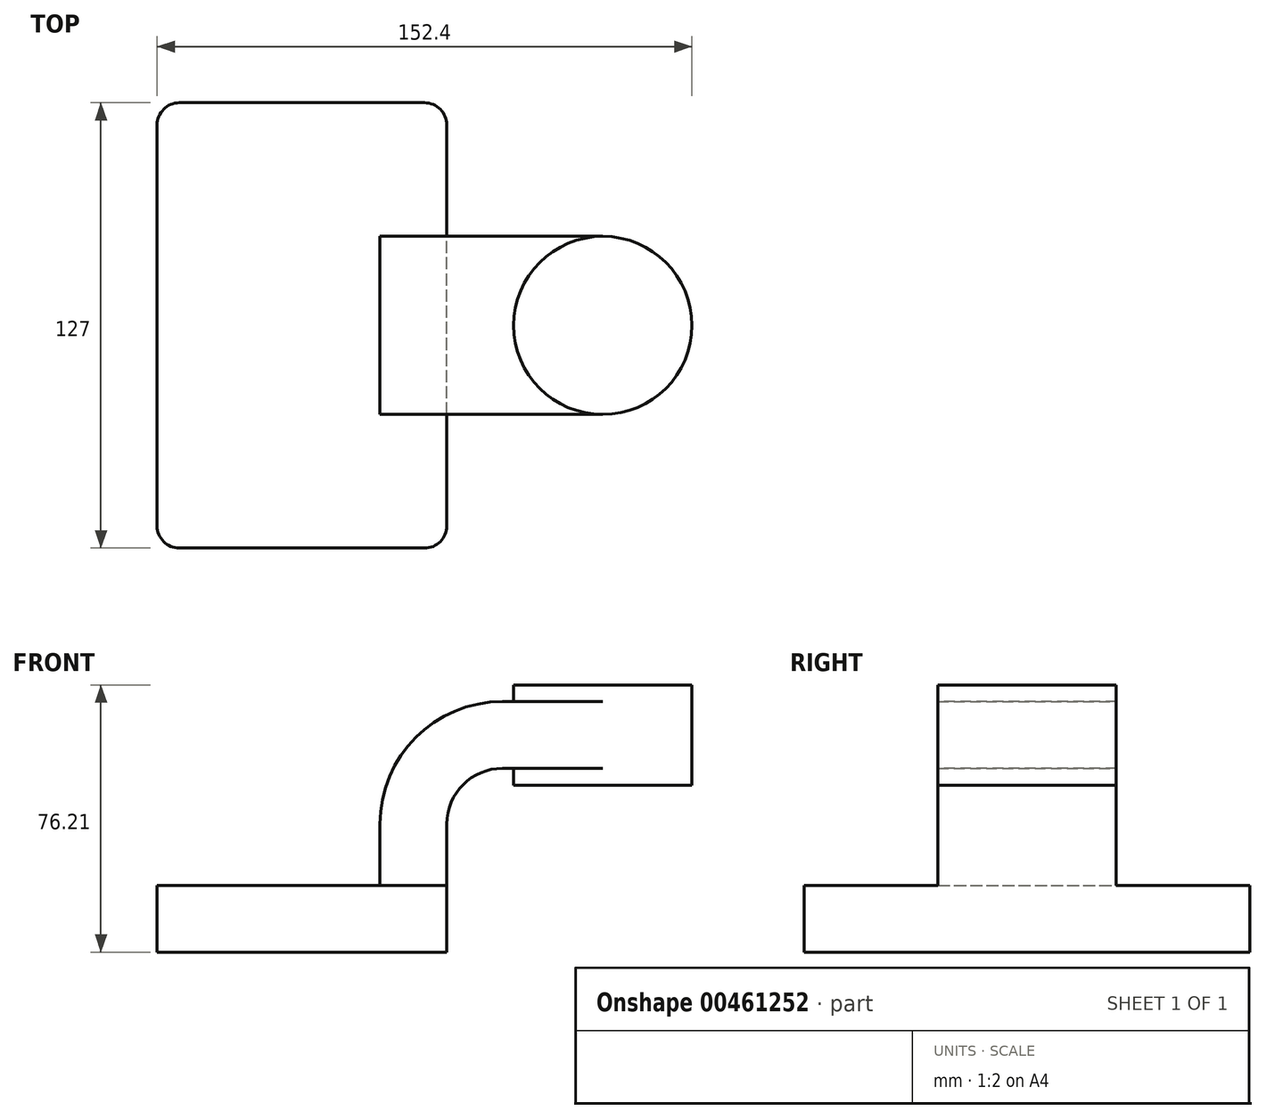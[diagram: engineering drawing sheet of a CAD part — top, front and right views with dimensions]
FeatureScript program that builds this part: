
annotation { "Feature Type Name" : "Feature", "Feature Type Description" : "" }
export const myFeature = defineFeature(function(context is Context, id is Id, definition is map)
    precondition{}
    {
        {
            var Q0;
            Q0=qCreatedBy(makeId("Front.planeOp"),FACE);
            var sketch = newSketch(context, id + "F0", { "sketchPlane" : qUnion([Q0])});
            skLineSegment(sketch, "E0.bottom", {"start": v(-41.27, -9.53) * mm, "end": v(41.28, -9.53) * mm});
            skLineSegment(sketch, "E0.top", {"start": v(-41.28, 9.53) * mm, "end": v(41.28, 9.53) * mm});
            skLineSegment(sketch, "E0.left", {"start": v(-41.28, -9.53) * mm, "end": v(-41.28, 9.53) * mm});
            skLineSegment(sketch, "E0.right", {"start": v(41.28, -9.53) * mm, "end": v(41.28, 9.52) * mm});
            skPoint(sketch, "E0.middle", {"position": v(0, 0) * mm});
            skLineSegment(sketch, "E1.bottom", {"start": v(111.12, 66.68) * mm, "end": v(60.32, 66.68) * mm});
            skLineSegment(sketch, "E1.top", {"start": v(111.12, 38.1) * mm, "end": v(60.33, 38.1) * mm});
            skLineSegment(sketch, "E1.left", {"start": v(111.12, 66.68) * mm, "end": v(111.12, 38.1) * mm});
            skLineSegment(sketch, "E1.right", {"start": v(60.33, 66.68) * mm, "end": v(60.33, 38.1) * mm});
            skPoint(sketch, "E1.middle", {"position": v(85.72, 52.39) * mm});
            skLineSegment(sketch, "E2", {"start": v(41.27, 9.52) * mm, "end": v(41.27, 27) * mm});
            skArc(sketch, "E3", {"start": v(41.27, 27) * mm, "mid": v(45.92, 38.23) * mm, "end": v(57.15, 42.88) * mm});
            skLineSegment(sketch, "E4", {"start": v(57.15, 42.88) * mm, "end": v(85.72, 42.88) * mm});
            skLineSegment(sketch, "E5.0", {"start": v(57.15, 61.93) * mm, "end": v(85.72, 61.93) * mm});
            skArc(sketch, "E5.1", {"start": v(22.23, 27) * mm, "mid": v(32.45, 51.7) * mm, "end": v(57.15, 61.93) * mm});
            skLineSegment(sketch, "E5.2", {"start": v(22.22, 9.52) * mm, "end": v(22.22, 27) * mm});
            skLineSegment(sketch, "E6", {"start": v(85.72, 61.93) * mm, "end": v(85.72, 42.88) * mm});
            skFitSpline(sketch, "E7", {"points": [v(-41.28, 9.53) * mm, v(57.15, 61.93) * mm], "startDerivative": vector(0.85, 40.24) * mm, "endDerivative": vector(110.8, -4.56) * mm});
            skLineSegment(sketch, "E8", {"start": v(85.72, 61.93) * mm, "end": v(85.72, 66.68) * mm});
            skLineSegment(sketch, "E9", {"start": v(85.72, 38.1) * mm, "end": v(85.72, 42.88) * mm});
            skSolve(sketch);
        }
        {
            var Q0;
            Q0=makeQuery(id+"F0.imprint","IMPRINT",FACE,{"disambiguationData":[TD([[makeQuery(id+"F0.imprint","IMPRINT",EDGE,{"derivedFrom":sQuery(id+"F0.wireOp",EDGE,"E0.bottom")}),1.0]])]});
            extrude(context, id + "F1", {"entities" : qUnion([Q0]), "endBound" : BoundingType.SYMMETRIC, "depth" : 127 * mm});
        }
        {
            var Q0;
            {var subQ0=sQuery(id+"F0.wireOp",EDGE,"E2");Q0=makeQuery(id+"F0.imprint","IMPRINT",FACE,{"disambiguationData":[TD([[makeQuery(id+"F0.imprint","IMPRINT",EDGE,{"derivedFrom":subQ0}),1.0]])]});}
            var Q1;
            {var subQ5=sQuery(id+"F0.wireOp",EDGE,"E6");Q1=makeQuery(id+"F0.imprint","IMPRINT",FACE,{"disambiguationData":[TD([[makeQuery(id+"F0.imprint","IMPRINT",EDGE,{"derivedFrom":subQ5}),-1.0]])]});}
            extrude(context, id + "F2", {"entities" : qUnion([Q0, Q1]), "operationType" : NewBodyOperationType.ADD, "endBound" : BoundingType.SYMMETRIC, "depth" : 50.8 * mm});
        }
        {
            var Q0;
            Q0=makeQuery(id+"F0.imprint","IMPRINT",FACE,{"disambiguationData":[TD([[makeQuery(id+"F0.imprint","IMPRINT",EDGE,{"derivedFrom":sQuery(id+"F0.wireOp",EDGE,"E5.1")}),1.0]])]});
            extrude(context, id + "F3", {"entities" : qUnion([Q0]), "operationType" : NewBodyOperationType.ADD, "endBound" : BoundingType.SYMMETRIC, "depth" : 15.88 * mm});
        }
        {
            var Q0;
            {var subQ0=sQuery(id+"F0.wireOp",EDGE,"E1.left");Q0=makeQuery(id+"F0.imprint","IMPRINT",FACE,{"disambiguationData":[TD([[makeQuery(id+"F0.imprint","IMPRINT",EDGE,{"derivedFrom":subQ0}),-1.0]])]});}
            var Q1;
            Q1=sQuery(id+"F0.wireOp",EDGE,"E6");
            revolve(context, id + "F4", {"operationType" : NewBodyOperationType.ADD, "entities" : qUnion([Q0]), "axis" : qUnion([Q1]), "revolveType" : RevolveType.FULL});
        }
        {
            var Q0;
            Q0=makeQuery(id+"F1.opExtrude","CAP_EDGE",EDGE,{"disambiguationData":[OSD([sQuery(id+"F0.wireOp",EDGE,"E0.right")])],"isStart":false});
            var Q1;
            Q1=makeQuery(id+"F1.opExtrude","CAP_EDGE",EDGE,{"disambiguationData":[OSD([sQuery(id+"F0.wireOp",EDGE,"E0.left")])],"isStart":false});
            var Q2;
            Q2=makeQuery(id+"F1.opExtrude","CAP_EDGE",EDGE,{"disambiguationData":[OSD([sQuery(id+"F0.wireOp",EDGE,"E0.right")])],"isStart":true});
            var Q3;
            Q3=makeQuery(id+"F1.opExtrude","CAP_EDGE",EDGE,{"disambiguationData":[OSD([sQuery(id+"F0.wireOp",EDGE,"E0.left")])],"isStart":true});
            fillet(context, id + "F5", {"entities" : qUnion([Q0, Q1, Q2, Q3]), "radius" : 6.35 * mm, "tangentPropagation" : true, "allowEdgeOverflow" : false});
        }
    });
